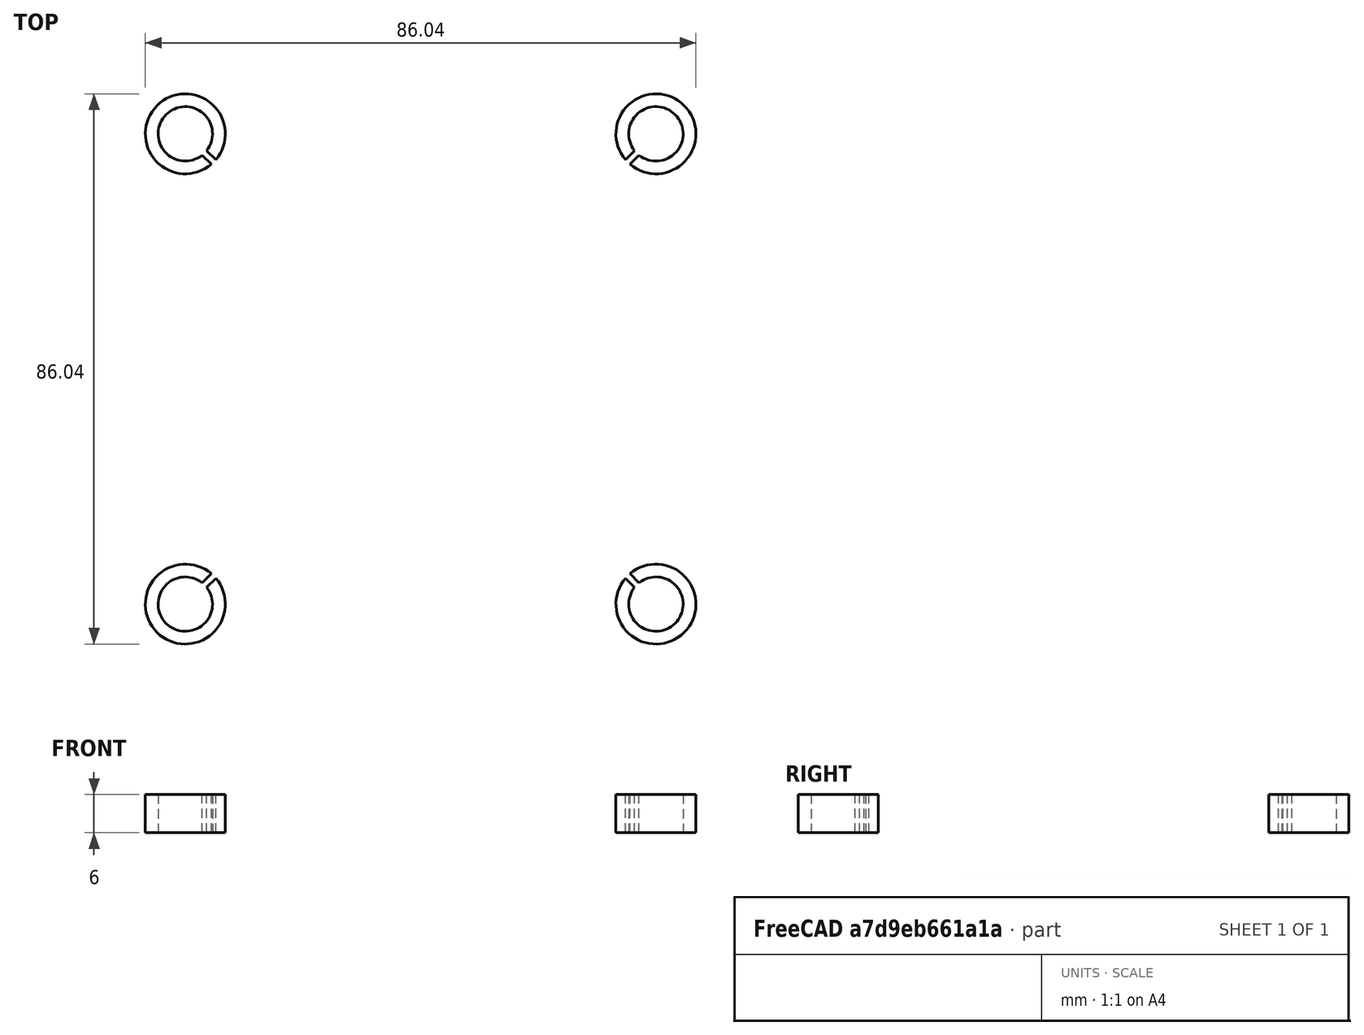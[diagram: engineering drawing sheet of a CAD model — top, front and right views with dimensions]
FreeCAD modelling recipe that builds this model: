
FCSTD DOCUMENT  (FreeCAD 0.19R23578 (Git))
Label: motors
License: All rights reserved
LicenseURL: http://en.wikipedia.org/wiki/All_rights_reserved
objects: Part::Feature×4, Part::Extrusion×4
note: 8 computed .brp shape members not serialized (recipe doc carries the construction recipe); baked Part::Feature solids carry a one-line shape summary decoded from their .brp

FEATURE [Part::Feature] Face
  shape: bbox 12.5 x 12.5 x 2e-07 mm, 1 faces, 0 solids (baked)
FEATURE [Part::Feature] Face001
  shape: bbox 12.5 x 12.5 x 2e-07 mm, 1 faces, 0 solids (baked)
FEATURE [Part::Feature] Face002
  shape: bbox 12.5 x 12.5 x 2e-07 mm, 1 faces, 0 solids (baked)
FEATURE [Part::Feature] Face003
  shape: bbox 12.5 x 12.5 x 2e-07 mm, 1 faces, 0 solids (baked)
FEATURE [Part::Extrusion] Extrude
  Base = -> Face
  Dir = (0,0,1)
  DirMode = 0
  FaceMakerClass = Part::FaceMakerBullseye
  LengthFwd = 6
  LengthRev = 0
  Solid = false
  Symmetric = false
FEATURE [Part::Extrusion] Extrude001
  Base = -> Face001
  Dir = (0,0,1)
  DirMode = 0
  FaceMakerClass = Part::FaceMakerBullseye
  LengthFwd = 6
  LengthRev = 0
  Solid = false
  Symmetric = false
FEATURE [Part::Extrusion] Extrude002
  Base = -> Face002
  Dir = (0,0,1)
  DirMode = 0
  FaceMakerClass = Part::FaceMakerBullseye
  LengthFwd = 6
  LengthRev = 0
  Solid = false
  Symmetric = false
FEATURE [Part::Extrusion] Extrude003
  Base = -> Face003
  Dir = (0,0,1)
  DirMode = 0
  FaceMakerClass = Part::FaceMakerBullseye
  LengthFwd = 6
  LengthRev = 0
  Solid = false
  Symmetric = false
